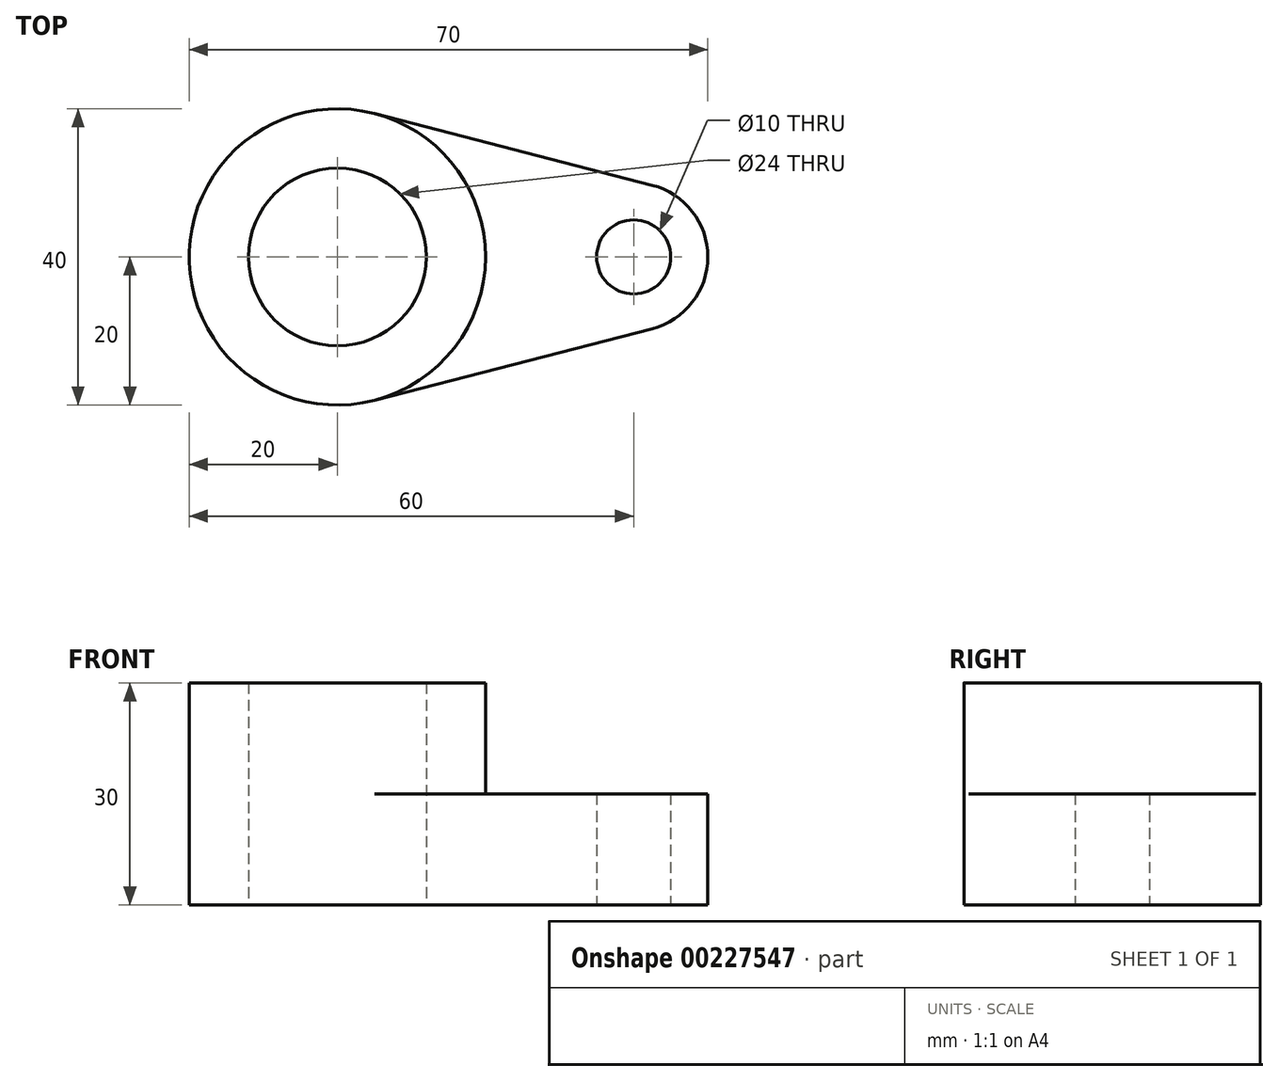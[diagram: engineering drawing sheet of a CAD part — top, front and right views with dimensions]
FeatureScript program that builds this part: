
annotation { "Feature Type Name" : "Feature", "Feature Type Description" : "" }
export const myFeature = defineFeature(function(context is Context, id is Id, definition is map)
    precondition{}
    {
        {
            var Q0;
            Q0=qCreatedBy(makeId("Top.planeOp"),FACE);
            var sketch = newSketch(context, id + "F0", { "sketchPlane" : qUnion([Q0])});
            skCircle(sketch, "E0", {"center": v(0, 0) * mm, "radius": 12 * mm});
            skCircle(sketch, "E1", {"center": v(0, 0) * mm, "radius": 20 * mm});
            skCircle(sketch, "E2", {"center": v(40, 0) * mm, "radius": 5 * mm});
            skArc(sketch, "E3", {"start": v(42.5, -9.68) * mm, "mid": v(50, 0) * mm, "end": v(42.5, 9.68) * mm});
            skLineSegment(sketch, "E4", {"start": v(5, 19.36) * mm, "end": v(42.5, 9.68) * mm});
            skLineSegment(sketch, "E5", {"start": v(5, -19.36) * mm, "end": v(42.5, -9.68) * mm});
            skSolve(sketch);
        }
        {
            var Q0;
            Q0=makeQuery(id+"F0.imprint","IMPRINT",FACE,{"disambiguationData":[TD([[makeQuery(id+"F0.imprint","IMPRINT",EDGE,{"derivedFrom":sQuery(id+"F0.wireOp",EDGE,"E2")}),-1.0]])]});
            extrude(context, id + "F1", {"entities" : qUnion([Q0]), "depth" : 15 * mm});
        }
        {
            var Q0;
            Q0=makeQuery(id+"F0.imprint","IMPRINT",FACE,{"disambiguationData":[TD([[makeQuery(id+"F0.imprint","IMPRINT",EDGE,{"derivedFrom":sQuery(id+"F0.wireOp",EDGE,"E0")}),-1.0]])]});
            extrude(context, id + "F2", {"entities" : qUnion([Q0]), "operationType" : NewBodyOperationType.ADD, "depth" : 30 * mm});
        }
    });
